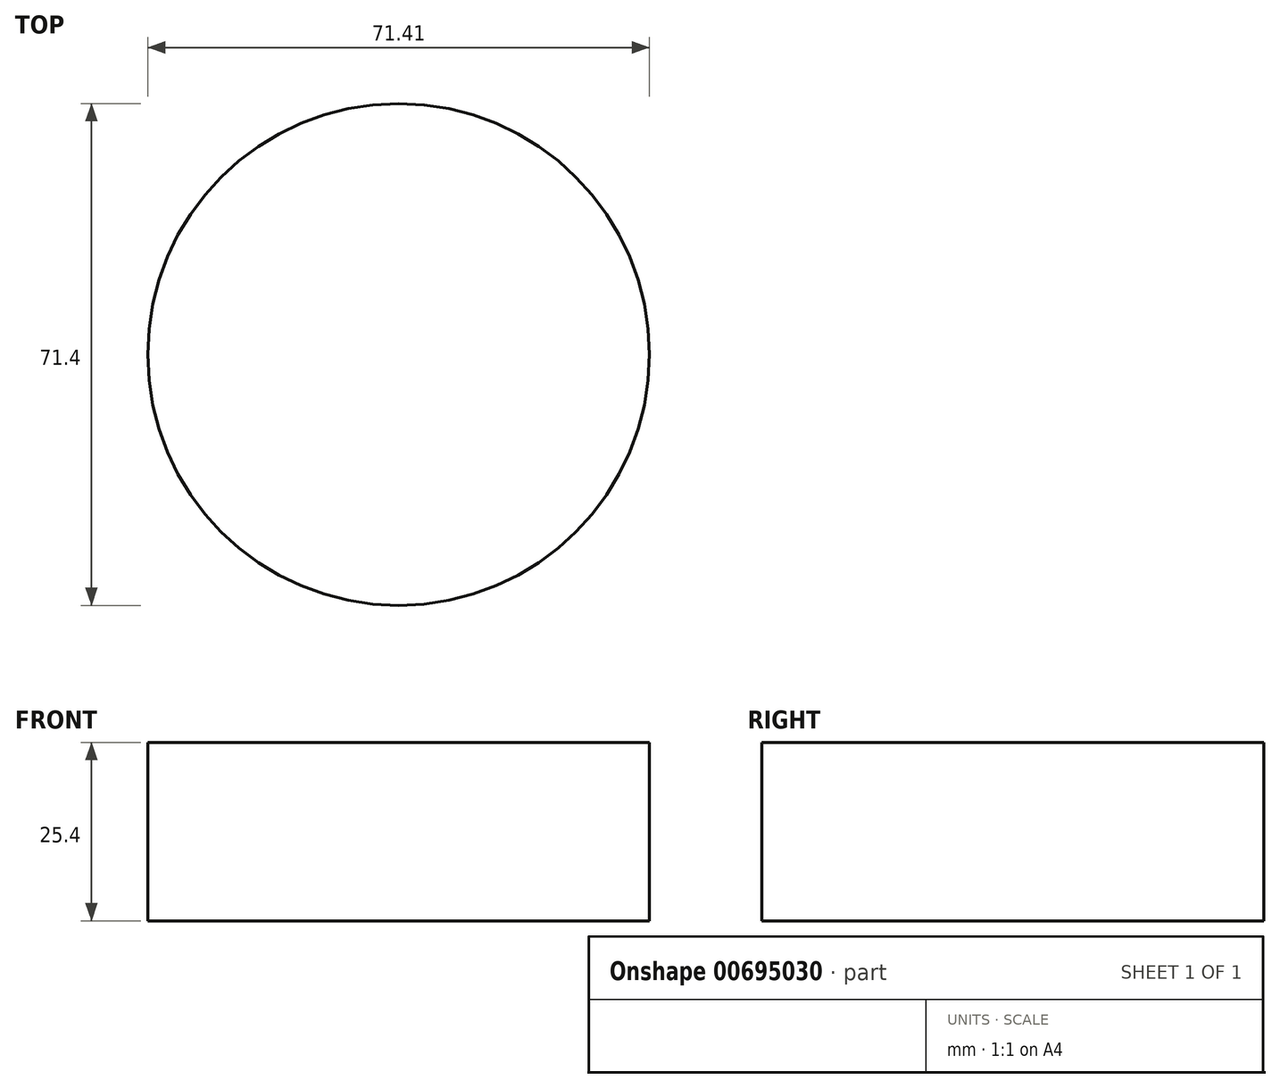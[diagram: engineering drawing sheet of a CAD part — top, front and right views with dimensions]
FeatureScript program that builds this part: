
annotation { "Feature Type Name" : "Feature", "Feature Type Description" : "" }
export const myFeature = defineFeature(function(context is Context, id is Id, definition is map)
    precondition{}
    {
        {
            var Q0;
            Q0=qCreatedBy(makeId("Top.planeOp"),FACE);
            var sketch = newSketch(context, id + "F0", { "sketchPlane" : qUnion([Q0])});
            skCircle(sketch, "E0", {"center": v(-27.81, 17.97) * mm, "radius": 35.7 * mm});
            skSolve(sketch);
        }
        {
            var Q0;
            Q0=makeQuery(id+"F0.imprint","IMPRINT",FACE,{"disambiguationData":[TD([[makeQuery(id+"F0.imprint","IMPRINT",EDGE,{"derivedFrom":sQuery(id+"F0.wireOp",EDGE,"E0")}),1.0]])]});
            extrude(context, id + "F1", {"entities" : qUnion([Q0]), "depth" : 25.4 * mm, "offsetDistance" : 25.4 * mm});
        }
    });
